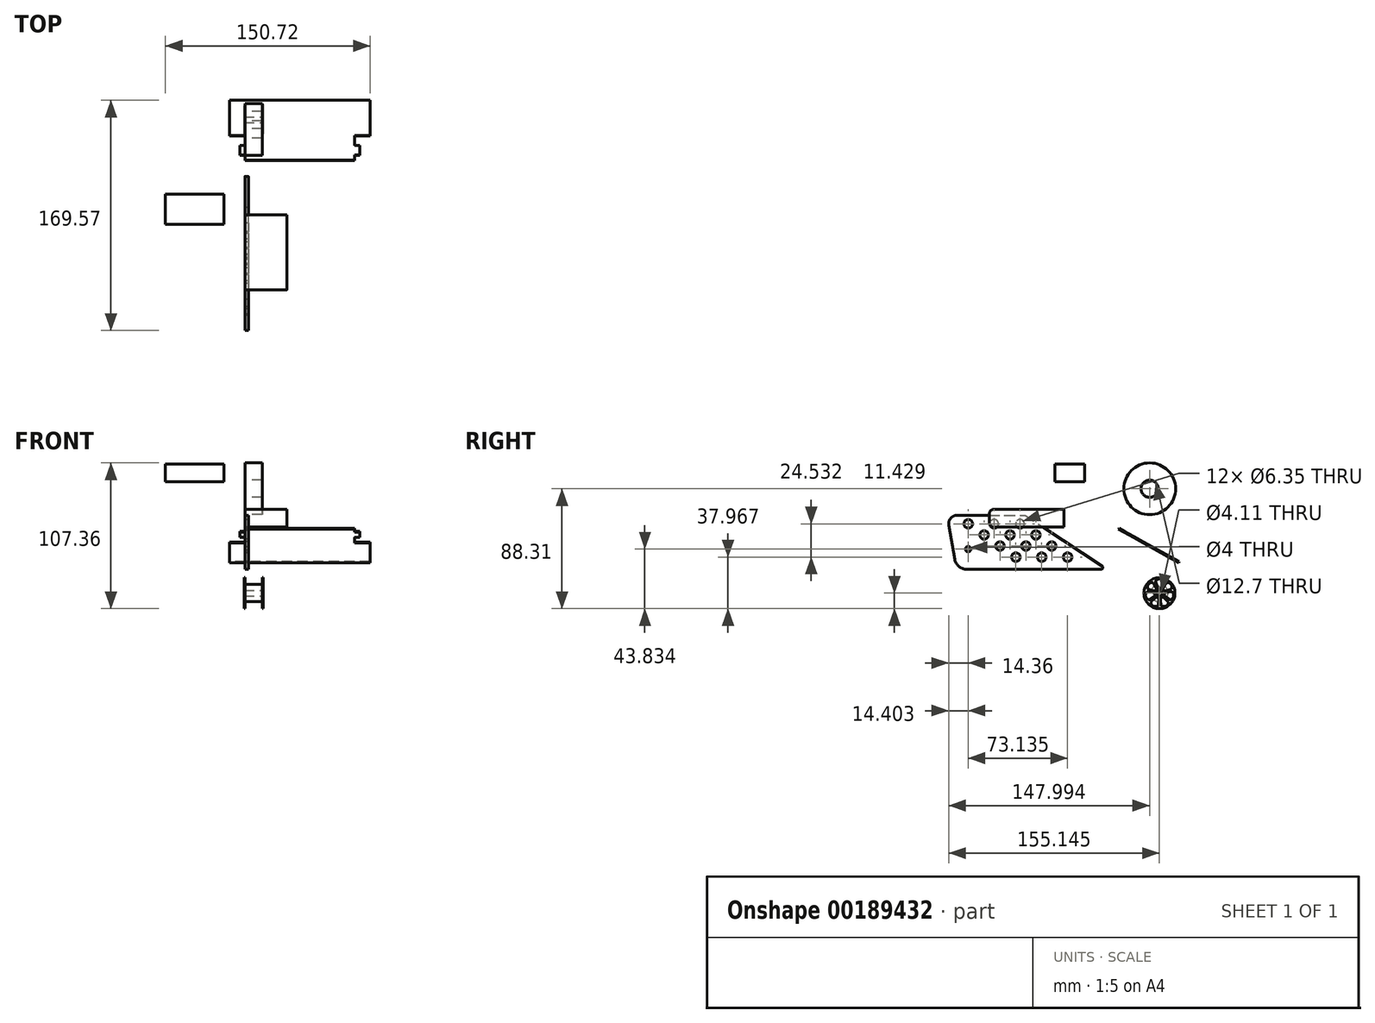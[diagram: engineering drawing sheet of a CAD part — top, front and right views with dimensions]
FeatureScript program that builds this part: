
annotation { "Feature Type Name" : "Feature", "Feature Type Description" : "" }
export const myFeature = defineFeature(function(context is Context, id is Id, definition is map)
    precondition{}
    {
        {
            var Q0;
            Q0=qCreatedBy(makeId("Right.planeOp"),FACE);
            var sketch = newSketch(context, id + "F0", { "sketchPlane" : qUnion([Q0])});
            skLineSegment(sketch, "E0.bottom", {"start": v(-67.05, 13) * mm, "end": v(-15.23, 13) * mm});
            skLineSegment(sketch, "E0.top", {"start": v(-67.05, 0) * mm, "end": v(-15.23, 0) * mm});
            skLineSegment(sketch, "E0.left", {"start": v(-70.23, 9.83) * mm, "end": v(-70.23, 3.18) * mm});
            skLineSegment(sketch, "E0.right", {"start": v(-15.23, 13) * mm, "end": v(-15.23, 0) * mm});
            skPoint(sketch, "E1.visualSharp", {"position": v(-70.23, 13) * mm});
            skArc(sketch, "E1.filletArc", {"start": v(-67.05, 13) * mm, "mid": v(-69.3, 12.07) * mm, "end": v(-70.23, 9.83) * mm});
            skPoint(sketch, "E2.visualSharp", {"position": v(-70.23, 0) * mm});
            skArc(sketch, "E2.filletArc", {"start": v(-70.23, 3.17) * mm, "mid": v(-69.3, 0.93) * mm, "end": v(-67.05, 0) * mm});
            skSolve(sketch);
        }
        {
            var Q0;
            Q0 = qSketchRegion(id + "F0", true);
            extrude(context, id + "F1", {"entities" : qUnion([Q0]), "depth" : 31 * mm});
        }
        {
            var Q0;
            Q0=qCreatedBy(makeId("Front.planeOp"),FACE);
            var sketch = newSketch(context, id + "F2", { "sketchPlane" : qUnion([Q0])});
            skLineSegment(sketch, "E3.bottom", {"start": v(-58.5, 46.23) * mm, "end": v(-15.5, 46.23) * mm});
            skLineSegment(sketch, "E3.top", {"start": v(-58.5, 33.23) * mm, "end": v(-15.5, 33.23) * mm});
            skLineSegment(sketch, "E3.left", {"start": v(-58.5, 46.23) * mm, "end": v(-58.5, 33.23) * mm});
            skLineSegment(sketch, "E3.right", {"start": v(-15.5, 46.23) * mm, "end": v(-15.5, 33.23) * mm});
            skSolve(sketch);
        }
        {
            var Q0;
            Q0 = qSketchRegion(id + "F2", true);
            extrude(context, id + "F3", {"entities" : qUnion([Q0]), "depth" : 22 * mm});
        }
        {
            var Q0;
            Q0=qCreatedBy(makeId("Right.planeOp"),FACE);
            var sketch = newSketch(context, id + "F4", { "sketchPlane" : qUnion([Q0])});
            skLineSegment(sketch, "E4.top", {"start": v(-86.98, -31.18) * mm, "end": v(-14.05, -31.18) * mm});
            skLineSegment(sketch, "E4.left", {"start": v(-100.15, 1.22) * mm, "end": v(-95.73, -23.84) * mm});
            skLineSegment(sketch, "E5", {"start": v(-43.97, 8.67) * mm, "end": v(16.25, -31.18) * mm});
            skLineSegment(sketch, "E6", {"start": v(16.25, -31.18) * mm, "end": v(-14.05, -31.18) * mm});
            skLineSegment(sketch, "E7", {"start": v(-93.9, 8.67) * mm, "end": v(-43.97, 8.67) * mm});
            skPoint(sketch, "E8.visualSharp", {"position": v(-94.44, -31.18) * mm});
            skArc(sketch, "E8.filletArc", {"start": v(-95.73, -23.84) * mm, "mid": v(-92.7, -29.1) * mm, "end": v(-86.98, -31.18) * mm});
            skCircle(sketch, "E9", {"center": v(-85.85, 2.35) * mm, "radius": 3.18 * mm});
            skCircle(sketch, "E10.0.1.0", {"center": v(-74.17, -5.83) * mm, "radius": 3.18 * mm});
            skCircle(sketch, "E10.1.0.0", {"center": v(-66.8, 2.35) * mm, "radius": 3.18 * mm});
            skCircle(sketch, "E10.1.1.0", {"center": v(-55.12, -5.83) * mm, "radius": 3.18 * mm});
            skLineSegment(sketch, "E10.direction1", {"start": v(-85.85, 2.35) * mm, "end": v(-66.8, 2.35) * mm, "construction": true});
            skLineSegment(sketch, "E10.direction2", {"start": v(-85.85, 2.35) * mm, "end": v(-74.17, -5.83) * mm, "construction": true});
            skCircle(sketch, "E11.0.2.0", {"center": v(-47.75, 2.35) * mm, "radius": 3.18 * mm});
            skCircle(sketch, "E11.0.2.1", {"center": v(-36.07, -5.83) * mm, "radius": 3.18 * mm});
            skCircle(sketch, "E12.0.0.2", {"center": v(-62.5, -14) * mm, "radius": 3.18 * mm});
            skCircle(sketch, "E12.0.1.2", {"center": v(-43.44, -14) * mm, "radius": 3.18 * mm});
            skCircle(sketch, "E12.0.2.2", {"center": v(-24.4, -14) * mm, "radius": 3.18 * mm});
            skPoint(sketch, "E13.visualSharp", {"position": v(-101.47, 8.67) * mm});
            skArc(sketch, "E13.filletArc", {"start": v(-93.9, 8.67) * mm, "mid": v(-98.76, 6.4) * mm, "end": v(-100.15, 1.22) * mm});
            skCircle(sketch, "E14.0.0.3", {"center": v(-50.81, -22.18) * mm, "radius": 3.18 * mm});
            skCircle(sketch, "E14.0.1.3", {"center": v(-31.76, -22.18) * mm, "radius": 3.18 * mm});
            skCircle(sketch, "E14.0.2.3", {"center": v(-12.71, -22.18) * mm, "radius": 3.18 * mm});
            skSolve(sketch);
        }
        {
            var Q0;
            Q0 = qSketchRegion(id + "F4", true);
            extrude(context, id + "F5", {"entities" : qUnion([Q0]), "depth" : 2.54 * mm});
        }
        {
            var Q0;
            Q0=makeQuery(id+"F5.opExtrude","SWEPT_EDGE",EDGE,{"disambiguationData":[OSD([sQuery(id+"F4.wireOp",EDGE,"E5"),sQuery(id+"F4.wireOp",EDGE,"E6")])]});
            fillet(context, id + "F6", {"entities" : qUnion([Q0]), "radius" : 1.27 * mm, "tangentPropagation" : true, "allowEdgeOverflow" : false});
        }
        {
            var Q0;
            Q0=qCreatedBy(makeId("Right.planeOp"),FACE);
            var sketch = newSketch(context, id + "F7", { "sketchPlane" : qUnion([Q0])});
            skCircle(sketch, "E15", {"center": v(47.74, 28.16) * mm, "radius": 19.05 * mm});
            skCircle(sketch, "E16", {"center": v(47.74, 28.16) * mm, "radius": 6.35 * mm});
            skSolve(sketch);
        }
        {
            var Q0;
            Q0 = qSketchRegion(id + "F7", true);
            extrude(context, id + "F8", {"entities" : qUnion([Q0]), "depth" : 12.7 * mm});
        }
        {
            var Q0;
            Q0=qCreatedBy(makeId("Right.planeOp"),FACE);
            var sketch = newSketch(context, id + "F9", { "sketchPlane" : qUnion([Q0])});
            skCircle(sketch, "E17", {"center": v(54.9, -48.72) * mm, "radius": 6.35 * mm});
            skSolve(sketch);
        }
        {
            var Q0;
            Q0 = qSketchRegion(id + "F9", true);
            extrude(context, id + "F10", {"entities" : qUnion([Q0]), "depth" : 12.7 * mm});
        }
        {
            var Q0;
            Q0=makeQuery(id+"F10.opExtrude","CAP_FACE",FACE,{"disambiguationData":[OSD([sQuery(id+"F9.wireOp",EDGE,"E17")])],"isStart":false});
            var sketch = newSketch(context, id + "F11", { "sketchPlane" : qUnion([Q0])});
            skCircle(sketch, "E18", {"center": v(54.9, -48.72) * mm, "radius": 11.43 * mm});
            skSolve(sketch);
        }
        {
            var Q0;
            Q0 = qSketchRegion(id + "F11", true);
            extrude(context, id + "F12", {"entities" : qUnion([Q0]), "operationType" : NewBodyOperationType.ADD, "depth" : 0.64 * mm});
        }
        {
            var Q0;
            Q0=makeQuery(id+"F10.opExtrude","CAP_FACE",FACE,{"disambiguationData":[OSD([sQuery(id+"F9.wireOp",EDGE,"E17")])],"isStart":true});
            var sketch = newSketch(context, id + "F13", { "sketchPlane" : qUnion([Q0])});
            skCircle(sketch, "E19", {"center": v(-54.9, -48.72) * mm, "radius": 11.43 * mm});
            skSolve(sketch);
        }
        {
            var Q0;
            Q0 = qSketchRegion(id + "F13", true);
            extrude(context, id + "F14", {"entities" : qUnion([Q0]), "operationType" : NewBodyOperationType.ADD, "depth" : 0.64 * mm});
        }
        {
            var Q0;
            Q0=makeQuery(id+"F12.opExtrude","CAP_FACE",FACE,{"disambiguationData":[OSD([sQuery(id+"F11.wireOp",EDGE,"E18")])],"isStart":false});
            var sketch = newSketch(context, id + "F15", { "sketchPlane" : qUnion([Q0])});
            skCircle(sketch, "E20", {"center": v(54.9, -48.72) * mm, "radius": 2.06 * mm});
            skSolve(sketch);
        }
        {
            var Q0;
            Q0 = qSketchRegion(id + "F15", true);
            extrude(context, id + "F16", {"entities" : qUnion([Q0]), "operationType" : NewBodyOperationType.REMOVE, "endBound" : BoundingType.THROUGH_ALL, "oppositeDirection" : true, "depth" : 25.4 * mm});
        }
        {
            var Q0;
            Q0=makeQuery(id+"F12.opExtrude","CAP_FACE",FACE,{"disambiguationData":[OSD([sQuery(id+"F11.wireOp",EDGE,"E18")])],"isStart":false});
            var sketch = newSketch(context, id + "F17", { "sketchPlane" : qUnion([Q0])});
            skLineSegment(sketch, "E21", {"start": v(55.06, -37.3) * mm, "end": v(55.06, -60.15) * mm});
            skArc(sketch, "E22", {"start": v(55.06, -38.2) * mm, "mid": v(56.87, -38.72) * mm, "end": v(58.13, -40.13) * mm});
            skLineSegment(sketch, "E23", {"start": v(58.13, -40.13) * mm, "end": v(56.65, -44.01) * mm});
            skArc(sketch, "E24.MirrorCS", {"start": v(55.06, -38.2) * mm, "mid": v(53.25, -38.72) * mm, "end": v(52, -40.13) * mm});
            skLineSegment(sketch, "E25.MirrorCS", {"start": v(52, -40.13) * mm, "end": v(53.46, -44.01) * mm});
            skArc(sketch, "E26", {"start": v(53.46, -44.01) * mm, "mid": v(55.06, -45.12) * mm, "end": v(56.65, -44.01) * mm});
            skArc(sketch, "E27.1.0", {"start": v(46.83, -42.16) * mm, "mid": v(46.11, -43.9) * mm, "end": v(46.43, -45.76) * mm});
            skLineSegment(sketch, "E27.1.1", {"start": v(46.43, -45.76) * mm, "end": v(50.38, -47.03) * mm});
            skArc(sketch, "E27.1.2", {"start": v(50.38, -47.03) * mm, "mid": v(52.24, -46.47) * mm, "end": v(52.37, -44.54) * mm});
            skLineSegment(sketch, "E27.1.3", {"start": v(50.26, -40.97) * mm, "end": v(52.37, -44.54) * mm});
            skArc(sketch, "E27.1.4", {"start": v(46.83, -42.16) * mm, "mid": v(48.37, -41.07) * mm, "end": v(50.26, -40.97) * mm});
            skArc(sketch, "E27.2.0", {"start": v(44.8, -51.06) * mm, "mid": v(45.71, -52.71) * mm, "end": v(47.37, -53.62) * mm});
            skLineSegment(sketch, "E27.2.1", {"start": v(47.37, -53.62) * mm, "end": v(50.82, -51.32) * mm});
            skArc(sketch, "E27.2.2", {"start": v(50.82, -51.32) * mm, "mid": v(51.54, -49.52) * mm, "end": v(50.12, -48.21) * mm});
            skLineSegment(sketch, "E27.2.3", {"start": v(46, -47.64) * mm, "end": v(50.12, -48.21) * mm});
            skArc(sketch, "E27.2.4", {"start": v(44.8, -51.06) * mm, "mid": v(44.9, -49.18) * mm, "end": v(46, -47.64) * mm});
            skPoint(sketch, "E27.center", {"position": v(55.06, -48.72) * mm});
            skArc(sketch, "E28.3.3.0", {"start": v(50.5, -58.2) * mm, "mid": v(52.35, -58.52) * mm, "end": v(54.1, -57.8) * mm});
            skLineSegment(sketch, "E28.4.3.0", {"start": v(54.1, -57.8) * mm, "end": v(54.45, -53.65) * mm});
            skArc(sketch, "E28.7.3.0", {"start": v(54.45, -53.65) * mm, "mid": v(53.5, -51.97) * mm, "end": v(51.58, -52.27) * mm});
            skLineSegment(sketch, "E28.11.3.0", {"start": v(48.57, -55.13) * mm, "end": v(51.58, -52.27) * mm});
            skArc(sketch, "E28.14.3.0", {"start": v(50.5, -58.2) * mm, "mid": v(49.09, -56.94) * mm, "end": v(48.57, -55.13) * mm});
            skArc(sketch, "E28.3.4.0", {"start": v(59.62, -58.2) * mm, "mid": v(61.03, -56.94) * mm, "end": v(61.55, -55.13) * mm});
            skLineSegment(sketch, "E28.4.4.0", {"start": v(61.55, -55.13) * mm, "end": v(58.54, -52.27) * mm});
            skArc(sketch, "E28.7.4.0", {"start": v(58.54, -52.27) * mm, "mid": v(56.62, -51.97) * mm, "end": v(55.66, -53.65) * mm});
            skLineSegment(sketch, "E28.11.4.0", {"start": v(56.02, -57.8) * mm, "end": v(55.66, -53.65) * mm});
            skArc(sketch, "E28.14.4.0", {"start": v(59.62, -58.2) * mm, "mid": v(57.76, -58.52) * mm, "end": v(56.02, -57.8) * mm});
            skArc(sketch, "E28.3.5.0", {"start": v(65.32, -51.06) * mm, "mid": v(65.2, -49.18) * mm, "end": v(64.12, -47.64) * mm});
            skLineSegment(sketch, "E28.4.5.0", {"start": v(64.12, -47.64) * mm, "end": v(60, -48.21) * mm});
            skArc(sketch, "E28.7.5.0", {"start": v(60, -48.21) * mm, "mid": v(58.57, -49.52) * mm, "end": v(59.3, -51.32) * mm});
            skLineSegment(sketch, "E28.11.5.0", {"start": v(62.75, -53.62) * mm, "end": v(59.3, -51.32) * mm});
            skArc(sketch, "E28.14.5.0", {"start": v(65.32, -51.06) * mm, "mid": v(64.4, -52.71) * mm, "end": v(62.75, -53.62) * mm});
            skArc(sketch, "E28.3.6.0", {"start": v(63.28, -42.16) * mm, "mid": v(61.75, -41.07) * mm, "end": v(59.86, -40.97) * mm});
            skLineSegment(sketch, "E28.4.6.0", {"start": v(59.86, -40.97) * mm, "end": v(57.74, -44.54) * mm});
            skArc(sketch, "E28.7.6.0", {"start": v(57.74, -44.54) * mm, "mid": v(57.88, -46.47) * mm, "end": v(59.73, -47.03) * mm});
            skLineSegment(sketch, "E28.11.6.0", {"start": v(63.69, -45.76) * mm, "end": v(59.73, -47.03) * mm});
            skArc(sketch, "E28.14.6.0", {"start": v(63.28, -42.16) * mm, "mid": v(64, -43.9) * mm, "end": v(63.69, -45.76) * mm});
            skSolve(sketch);
        }
        {
            var Q0;
            Q0 = qSketchRegion(id + "F17", true);
            extrude(context, id + "F18", {"entities" : qUnion([Q0]), "operationType" : NewBodyOperationType.REMOVE, "oppositeDirection" : true, "depth" : 0.23 * mm});
        }
        {
            var Q0;
            Q0=makeQuery(id+"F14.opExtrude","CAP_FACE",FACE,{"disambiguationData":[OSD([sQuery(id+"F13.wireOp",EDGE,"E19")])],"isStart":false});
            var sketch = newSketch(context, id + "F19", { "sketchPlane" : qUnion([Q0])});
            skLineSegment(sketch, "E29", {"start": v(-54.9, -37.57) * mm, "end": v(-54.9, -59.87) * mm});
            skArc(sketch, "E30", {"start": v(-54.9, -38.17) * mm, "mid": v(-53.05, -38.78) * mm, "end": v(-51.93, -40.36) * mm});
            skLineSegment(sketch, "E31", {"start": v(-51.93, -40.36) * mm, "end": v(-53.32, -43.78) * mm});
            skArc(sketch, "E32.MirrorCS", {"start": v(-54.9, -38.17) * mm, "mid": v(-56.74, -38.78) * mm, "end": v(-57.86, -40.36) * mm});
            skLineSegment(sketch, "E33.MirrorCS", {"start": v(-57.86, -40.36) * mm, "end": v(-56.47, -43.78) * mm});
            skArc(sketch, "E34", {"start": v(-56.47, -43.78) * mm, "mid": v(-54.9, -44.84) * mm, "end": v(-53.32, -43.78) * mm});
            skArc(sketch, "E35.1.0", {"start": v(-63.14, -42.15) * mm, "mid": v(-63.82, -43.97) * mm, "end": v(-63.28, -45.83) * mm});
            skLineSegment(sketch, "E35.1.1", {"start": v(-63.28, -45.83) * mm, "end": v(-59.75, -46.87) * mm});
            skArc(sketch, "E35.1.2", {"start": v(-59.75, -46.87) * mm, "mid": v(-57.93, -46.3) * mm, "end": v(-57.78, -44.4) * mm});
            skLineSegment(sketch, "E35.1.3", {"start": v(-59.58, -41.19) * mm, "end": v(-57.78, -44.4) * mm});
            skArc(sketch, "E35.1.4", {"start": v(-63.14, -42.15) * mm, "mid": v(-61.52, -41.08) * mm, "end": v(-59.58, -41.19) * mm});
            skArc(sketch, "E35.2.0", {"start": v(-65.18, -51.07) * mm, "mid": v(-64.18, -52.73) * mm, "end": v(-62.38, -53.48) * mm});
            skLineSegment(sketch, "E35.2.1", {"start": v(-62.38, -53.48) * mm, "end": v(-59.37, -51.36) * mm});
            skArc(sketch, "E35.2.2", {"start": v(-59.37, -51.36) * mm, "mid": v(-58.68, -49.59) * mm, "end": v(-60.07, -48.28) * mm});
            skLineSegment(sketch, "E35.2.3", {"start": v(-63.7, -47.69) * mm, "end": v(-60.07, -48.28) * mm});
            skArc(sketch, "E35.2.4", {"start": v(-65.18, -51.07) * mm, "mid": v(-65, -49.13) * mm, "end": v(-63.7, -47.69) * mm});
            skPoint(sketch, "E35.center", {"position": v(-54.9, -48.72) * mm});
            skArc(sketch, "E36.3.3.0", {"start": v(-59.47, -58.22) * mm, "mid": v(-57.55, -58.48) * mm, "end": v(-55.85, -57.54) * mm});
            skLineSegment(sketch, "E36.4.3.0", {"start": v(-55.85, -57.54) * mm, "end": v(-55.62, -53.86) * mm});
            skArc(sketch, "E36.7.3.0", {"start": v(-55.62, -53.86) * mm, "mid": v(-56.58, -52.22) * mm, "end": v(-58.46, -52.5) * mm});
            skLineSegment(sketch, "E36.11.3.0", {"start": v(-61.2, -54.96) * mm, "end": v(-58.46, -52.5) * mm});
            skArc(sketch, "E36.14.3.0", {"start": v(-59.47, -58.22) * mm, "mid": v(-60.87, -56.88) * mm, "end": v(-61.2, -54.96) * mm});
            skArc(sketch, "E36.3.4.0", {"start": v(-50.32, -58.22) * mm, "mid": v(-48.92, -56.88) * mm, "end": v(-48.6, -54.96) * mm});
            skLineSegment(sketch, "E36.4.4.0", {"start": v(-48.6, -54.96) * mm, "end": v(-51.33, -52.5) * mm});
            skArc(sketch, "E36.7.4.0", {"start": v(-51.33, -52.5) * mm, "mid": v(-53.21, -52.22) * mm, "end": v(-54.17, -53.86) * mm});
            skLineSegment(sketch, "E36.11.4.0", {"start": v(-53.94, -57.54) * mm, "end": v(-54.17, -53.86) * mm});
            skArc(sketch, "E36.14.4.0", {"start": v(-50.32, -58.22) * mm, "mid": v(-52.24, -58.48) * mm, "end": v(-53.94, -57.54) * mm});
            skArc(sketch, "E36.3.5.0", {"start": v(-44.61, -51.07) * mm, "mid": v(-44.8, -49.13) * mm, "end": v(-46.09, -47.69) * mm});
            skLineSegment(sketch, "E36.4.5.0", {"start": v(-46.09, -47.69) * mm, "end": v(-49.72, -48.28) * mm});
            skArc(sketch, "E36.7.5.0", {"start": v(-49.72, -48.28) * mm, "mid": v(-51.1, -49.59) * mm, "end": v(-50.43, -51.36) * mm});
            skLineSegment(sketch, "E36.11.5.0", {"start": v(-47.4, -53.48) * mm, "end": v(-50.43, -51.36) * mm});
            skArc(sketch, "E36.14.5.0", {"start": v(-44.61, -51.07) * mm, "mid": v(-45.62, -52.73) * mm, "end": v(-47.4, -53.48) * mm});
            skArc(sketch, "E36.3.6.0", {"start": v(-46.65, -42.15) * mm, "mid": v(-48.27, -41.08) * mm, "end": v(-50.21, -41.19) * mm});
            skLineSegment(sketch, "E36.4.6.0", {"start": v(-50.21, -41.19) * mm, "end": v(-52.01, -44.4) * mm});
            skArc(sketch, "E36.7.6.0", {"start": v(-52.01, -44.4) * mm, "mid": v(-51.86, -46.3) * mm, "end": v(-50.04, -46.87) * mm});
            skLineSegment(sketch, "E36.11.6.0", {"start": v(-46.51, -45.83) * mm, "end": v(-50.04, -46.87) * mm});
            skArc(sketch, "E36.14.6.0", {"start": v(-46.65, -42.15) * mm, "mid": v(-45.97, -43.97) * mm, "end": v(-46.51, -45.83) * mm});
            skSolve(sketch);
        }
        {
            var Q0;
            Q0 = qSketchRegion(id + "F19", true);
            extrude(context, id + "F20", {"entities" : qUnion([Q0]), "operationType" : NewBodyOperationType.REMOVE, "oppositeDirection" : true, "depth" : 0.23 * mm});
        }
        {
            var Q0;
            Q0=makeQuery(id+"F5.opExtrude","CAP_FACE",FACE,{"disambiguationData":[OSD([sQuery(id+"F4.wireOp",EDGE,"E4.top"),sQuery(id+"F4.wireOp",EDGE,"E4.left"),sQuery(id+"F4.wireOp",EDGE,"E5"),sQuery(id+"F4.wireOp",EDGE,"E6"),sQuery(id+"F4.wireOp",EDGE,"E7"),sQuery(id+"F4.wireOp",EDGE,"E8.filletArc"),sQuery(id+"F4.wireOp",EDGE,"E9"),sQuery(id+"F4.wireOp",EDGE,"E10.0.1.0"),sQuery(id+"F4.wireOp",EDGE,"E10.1.0.0"),sQuery(id+"F4.wireOp",EDGE,"E10.1.1.0"),sQuery(id+"F4.wireOp",EDGE,"E10.2.0.0"),sQuery(id+"F4.wireOp",EDGE,"E10.2.1.0"),sQuery(id+"F4.wireOp",EDGE,"d53a4eb9-0ef7-4ed4-bb3e-3d66f3efa5a4.0.3.0"),sQuery(id+"F4.wireOp",EDGE,"d53a4eb9-0ef7-4ed4-bb3e-3d66f3efa5a4.0.3.1")])],"isStart":false});
            var sketch = newSketch(context, id + "F21", { "sketchPlane" : qUnion([Q0])});
            skCircle(sketch, "E37", {"center": v(-85.89, -16.32) * mm, "radius": 2 * mm});
            skSolve(sketch);
        }
        {
            var Q0;
            Q0 = qSketchRegion(id + "F21", true);
            extrude(context, id + "F22", {"entities" : qUnion([Q0]), "operationType" : NewBodyOperationType.REMOVE, "endBound" : BoundingType.THROUGH_ALL, "oppositeDirection" : true, "depth" : 25.4 * mm});
        }
        {
            var Q0;
            Q0=qCreatedBy(makeId("Right.planeOp"),FACE);
            var sketch = newSketch(context, id + "F23", { "sketchPlane" : qUnion([Q0])});
            skLineSegment(sketch, "E38", {"start": v(24.76, -1.62) * mm, "end": v(68.95, -26.2) * mm});
            skLineSegment(sketch, "E39.0", {"start": v(25.13, -0.95) * mm, "end": v(69.32, -25.54) * mm});
            skLineSegment(sketch, "E40", {"start": v(25.13, -0.95) * mm, "end": v(24.76, -1.62) * mm});
            skLineSegment(sketch, "E41", {"start": v(69.32, -25.54) * mm, "end": v(68.95, -26.2) * mm});
            skSolve(sketch);
        }
        {
            var Q0;
            Q0 = qSketchRegion(id + "F23", true);
            extrude(context, id + "F24", {"entities" : qUnion([Q0]), "depth" : 80.8 * mm});
        }
        {
            var Q0;
            Q0=makeQuery(id+"F24.opExtrude","CAP_FACE",FACE,{"disambiguationData":[OSD([sQuery(id+"F23.wireOp",EDGE,"E38"),sQuery(id+"F23.wireOp",EDGE,"E39.0"),sQuery(id+"F23.wireOp",EDGE,"E40"),sQuery(id+"F23.wireOp",EDGE,"E41")])],"isStart":false});
            var sketch = newSketch(context, id + "F25", { "sketchPlane" : qUnion([Q0])});
            skLineSegment(sketch, "E42", {"start": v(43.46, -11.15) * mm, "end": v(43.09, -11.82) * mm});
            skLineSegment(sketch, "E43", {"start": v(43.09, -11.82) * mm, "end": v(68.95, -26.2) * mm});
            skLineSegment(sketch, "E44", {"start": v(68.95, -26.2) * mm, "end": v(69.32, -25.54) * mm});
            skLineSegment(sketch, "E45", {"start": v(69.32, -25.54) * mm, "end": v(43.46, -11.15) * mm});
            skSolve(sketch);
        }
        {
            var Q0;
            Q0 = qSketchRegion(id + "F25", true);
            extrude(context, id + "F26", {"entities" : qUnion([Q0]), "operationType" : NewBodyOperationType.ADD, "depth" : 11.43 * mm});
        }
        {
            var Q0;
            Q0=makeQuery(id+"F26.boolean.opBoolean","MERGE",FACE,{"derivedFrom":[makeQuery(id+"F24.opExtrude","SWEPT_FACE",FACE,{"disambiguationData":[OSD([sQuery(id+"F23.wireOp",EDGE,"E39.0")])]}),makeQuery(id+"F26.opExtrude","SWEPT_FACE",FACE,{"disambiguationData":[OSD([sQuery(id+"F25.wireOp",EDGE,"E45")])]})]});
            var sketch = newSketch(context, id + "F27", { "sketchPlane" : qUnion([Q0])});
            skLineSegment(sketch, "E46", {"start": v(0, 43.4) * mm, "end": v(-11.43, 43.4) * mm});
            skLineSegment(sketch, "E47", {"start": v(-11.43, 43.4) * mm, "end": v(-11.43, 73) * mm});
            skLineSegment(sketch, "E48", {"start": v(-11.43, 73) * mm, "end": v(0, 73) * mm});
            skLineSegment(sketch, "E49.bottom", {"start": v(80.8, 26.85) * mm, "end": v(84.6, 26.85) * mm});
            skLineSegment(sketch, "E49.top", {"start": v(80.8, 34.85) * mm, "end": v(84.6, 34.85) * mm});
            skLineSegment(sketch, "E49.left", {"start": v(80.8, 26.85) * mm, "end": v(80.8, 34.85) * mm});
            skLineSegment(sketch, "E49.right", {"start": v(84.6, 26.85) * mm, "end": v(84.6, 34.85) * mm});
            skLineSegment(sketch, "E50.bottom", {"start": v(0, 26.85) * mm, "end": v(-3.81, 26.85) * mm});
            skLineSegment(sketch, "E50.top", {"start": v(0, 34.85) * mm, "end": v(-3.81, 34.85) * mm});
            skLineSegment(sketch, "E50.left", {"start": v(0, 26.85) * mm, "end": v(0, 34.85) * mm});
            skLineSegment(sketch, "E50.right", {"start": v(-3.8, 26.85) * mm, "end": v(-3.81, 34.85) * mm});
            skSolve(sketch);
        }
        {
            var Q0;
            {var subQ0=sQuery(id+"F27.wireOp",EDGE,"E46");Q0=makeQuery(id+"F27.imprint","IMPRINT",FACE,{"disambiguationData":[TD([[makeQuery(id+"F27.imprint","IMPRINT",EDGE,{"derivedFrom":subQ0}),-1.0]])]});}
            var Q1;
            Q1=makeQuery(id+"F27.imprint","IMPRINT",FACE,{"disambiguationData":[TD([[makeQuery(id+"F27.imprint","IMPRINT",EDGE,{"derivedFrom":sQuery(id+"F27.wireOp",EDGE,"E49.bottom")}),1.0]])]});
            var Q2;
            Q2=makeQuery(id+"F27.imprint","IMPRINT",FACE,{"disambiguationData":[TD([[makeQuery(id+"F27.imprint","IMPRINT",EDGE,{"derivedFrom":sQuery(id+"F27.wireOp",EDGE,"E50.bottom")}),-1.0]])]});
            extrude(context, id + "F28", {"entities" : qUnion([Q0, Q1, Q2]), "operationType" : NewBodyOperationType.ADD, "oppositeDirection" : true, "depth" : 0.76 * mm});
        }
    });
